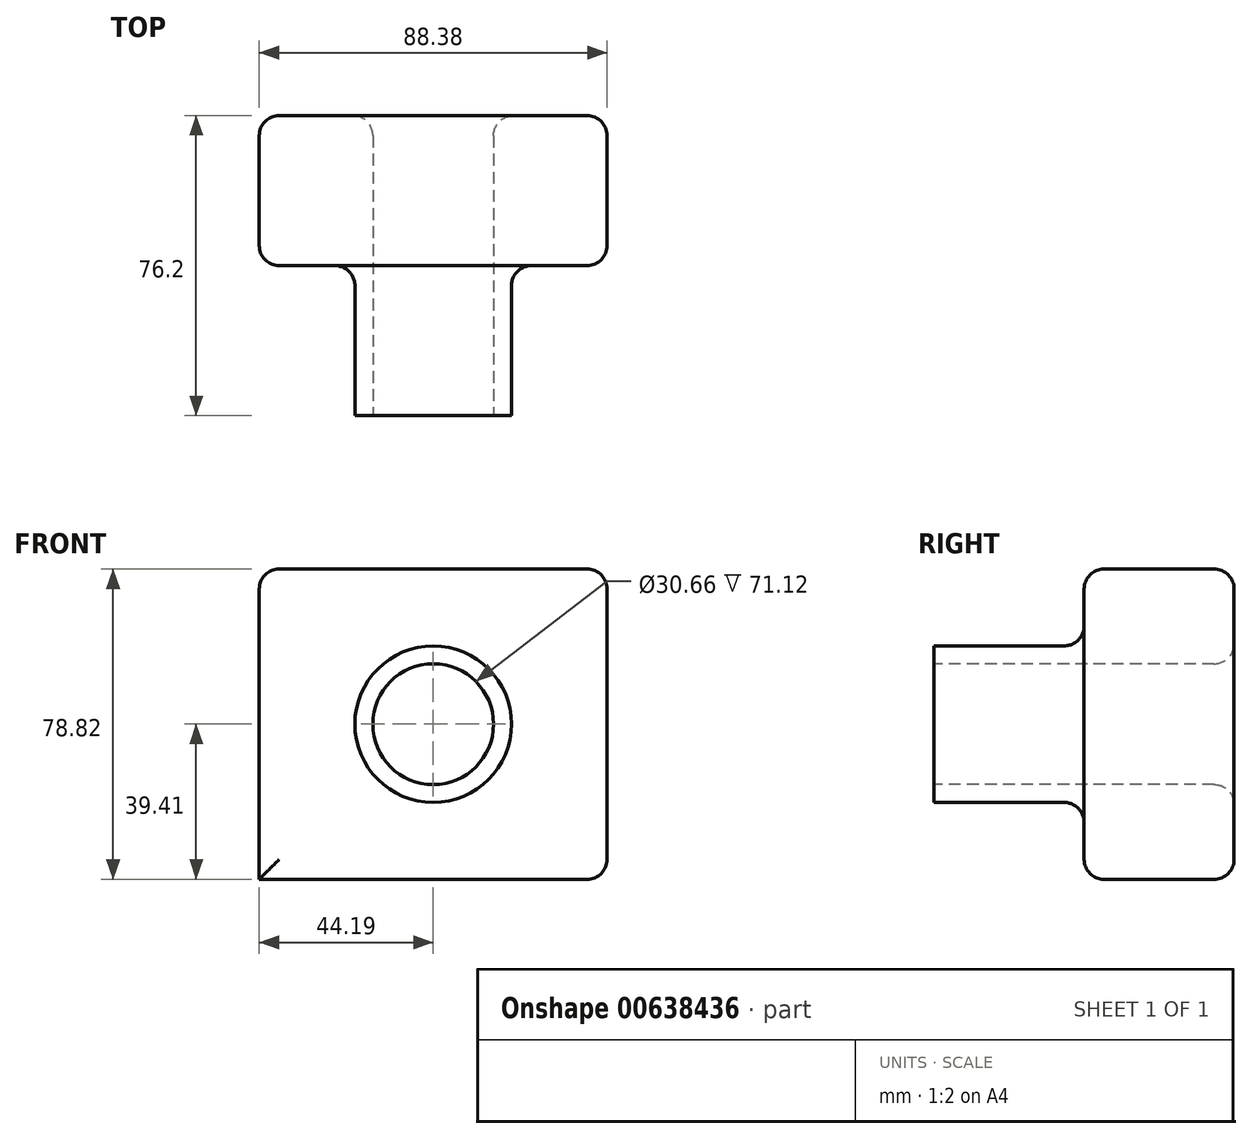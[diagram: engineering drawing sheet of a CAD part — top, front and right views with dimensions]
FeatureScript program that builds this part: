
annotation { "Feature Type Name" : "Feature", "Feature Type Description" : "" }
export const myFeature = defineFeature(function(context is Context, id is Id, definition is map)
    precondition{}
    {
        {
            var Q0;
            Q0=qCreatedBy(makeId("Front.planeOp"),FACE);
            var sketch = newSketch(context, id + "F0", { "sketchPlane" : qUnion([Q0])});
            skLineSegment(sketch, "E0.bottom", {"start": v(-44.19, 39.41) * mm, "end": v(44.19, 39.41) * mm});
            skLineSegment(sketch, "E0.top", {"start": v(-44.19, -39.41) * mm, "end": v(44.19, -39.41) * mm});
            skLineSegment(sketch, "E0.left", {"start": v(-44.19, 39.41) * mm, "end": v(-44.19, -39.41) * mm});
            skLineSegment(sketch, "E0.right", {"start": v(44.19, 39.41) * mm, "end": v(44.19, -39.41) * mm});
            skPoint(sketch, "E0.middle", {"position": v(0, 0) * mm});
            skSolve(sketch);
        }
        {
            var Q0;
            Q0=makeQuery(id+"F0.imprint","IMPRINT",FACE,{"disambiguationData":[TD([[makeQuery(id+"F0.imprint","IMPRINT",EDGE,{"derivedFrom":sQuery(id+"F0.wireOp",EDGE,"E0.bottom")}),-1.0]])]});
            extrude(context, id + "F1", {"entities" : qUnion([Q0]), "depth" : 38.1 * mm, "offsetDistance" : 25.4 * mm});
        }
        {
            var Q0;
            Q0=qCreatedBy(makeId("Front.planeOp"),FACE);
            var sketch = newSketch(context, id + "F2", { "sketchPlane" : qUnion([Q0])});
            skCircle(sketch, "E1", {"center": v(0, 0) * mm, "radius": 19.89 * mm});
            skSolve(sketch);
        }
        {
            var Q0;
            Q0 = qSketchRegion(id + "F2", true);
            extrude(context, id + "F3", {"entities" : qUnion([Q0]), "operationType" : NewBodyOperationType.ADD, "depth" : 76.2 * mm, "offsetDistance" : 25.4 * mm});
        }
        {
            var Q0;
            Q0=makeQuery(id+"F3.opExtrude","CAP_FACE",FACE,{"disambiguationData":[OSD([sQuery(id+"F2.wireOp",EDGE,"E1")])],"isStart":false});
            var sketch = newSketch(context, id + "F4", { "sketchPlane" : qUnion([Q0])});
            skCircle(sketch, "E2", {"center": v(0, 0) * mm, "radius": 15.33 * mm});
            skSolve(sketch);
        }
        {
            var Q0;
            Q0=makeQuery(id+"F4.imprint","IMPRINT",FACE,{"disambiguationData":[TD([[makeQuery(id+"F4.imprint","IMPRINT",EDGE,{"derivedFrom":sQuery(id+"F4.wireOp",EDGE,"E2")}),1.0]])]});
            extrude(context, id + "F5", {"entities" : qUnion([Q0]), "operationType" : NewBodyOperationType.REMOVE, "oppositeDirection" : true, "depth" : 101.6 * mm, "offsetDistance" : 25.4 * mm});
        }
        {
            var Q0;
            Q0=makeQuery(id+"F1.opExtrude","SWEPT_EDGE",EDGE,{"disambiguationData":[OSD([sQuery(id+"F0.wireOp",EDGE,"E0.bottom"),sQuery(id+"F0.wireOp",EDGE,"E0.left")])]});
            var Q1;
            Q1=makeQuery(id+"F1.opExtrude","CAP_EDGE",EDGE,{"disambiguationData":[OSD([sQuery(id+"F0.wireOp",EDGE,"E0.bottom")])],"isStart":true});
            var Q2;
            Q2=makeQuery(id+"F1.opExtrude","CAP_FACE",FACE,{"disambiguationData":[OSD([sQuery(id+"F0.wireOp",EDGE,"E0.bottom"),sQuery(id+"F0.wireOp",EDGE,"E0.top"),sQuery(id+"F0.wireOp",EDGE,"E0.left"),sQuery(id+"F0.wireOp",EDGE,"E0.right")])],"isStart":false});
            var Q3;
            Q3=makeQuery(id+"F1.opExtrude","SWEPT_FACE",FACE,{"disambiguationData":[OSD([sQuery(id+"F0.wireOp",EDGE,"E0.right")])]});
            var Q4;
            Q4=makeQuery(id+"F1.opExtrude","CAP_FACE",FACE,{"disambiguationData":[OSD([sQuery(id+"F0.wireOp",EDGE,"E0.bottom"),sQuery(id+"F0.wireOp",EDGE,"E0.top"),sQuery(id+"F0.wireOp",EDGE,"E0.left"),sQuery(id+"F0.wireOp",EDGE,"E0.right")])],"isStart":true});
            fillet(context, id + "F6", {"entities" : qUnion([Q0, Q1, Q2, Q3, Q4]), "radius" : 5.08 * mm, "tangentPropagation" : true, "allowEdgeOverflow" : false});
        }
    });
